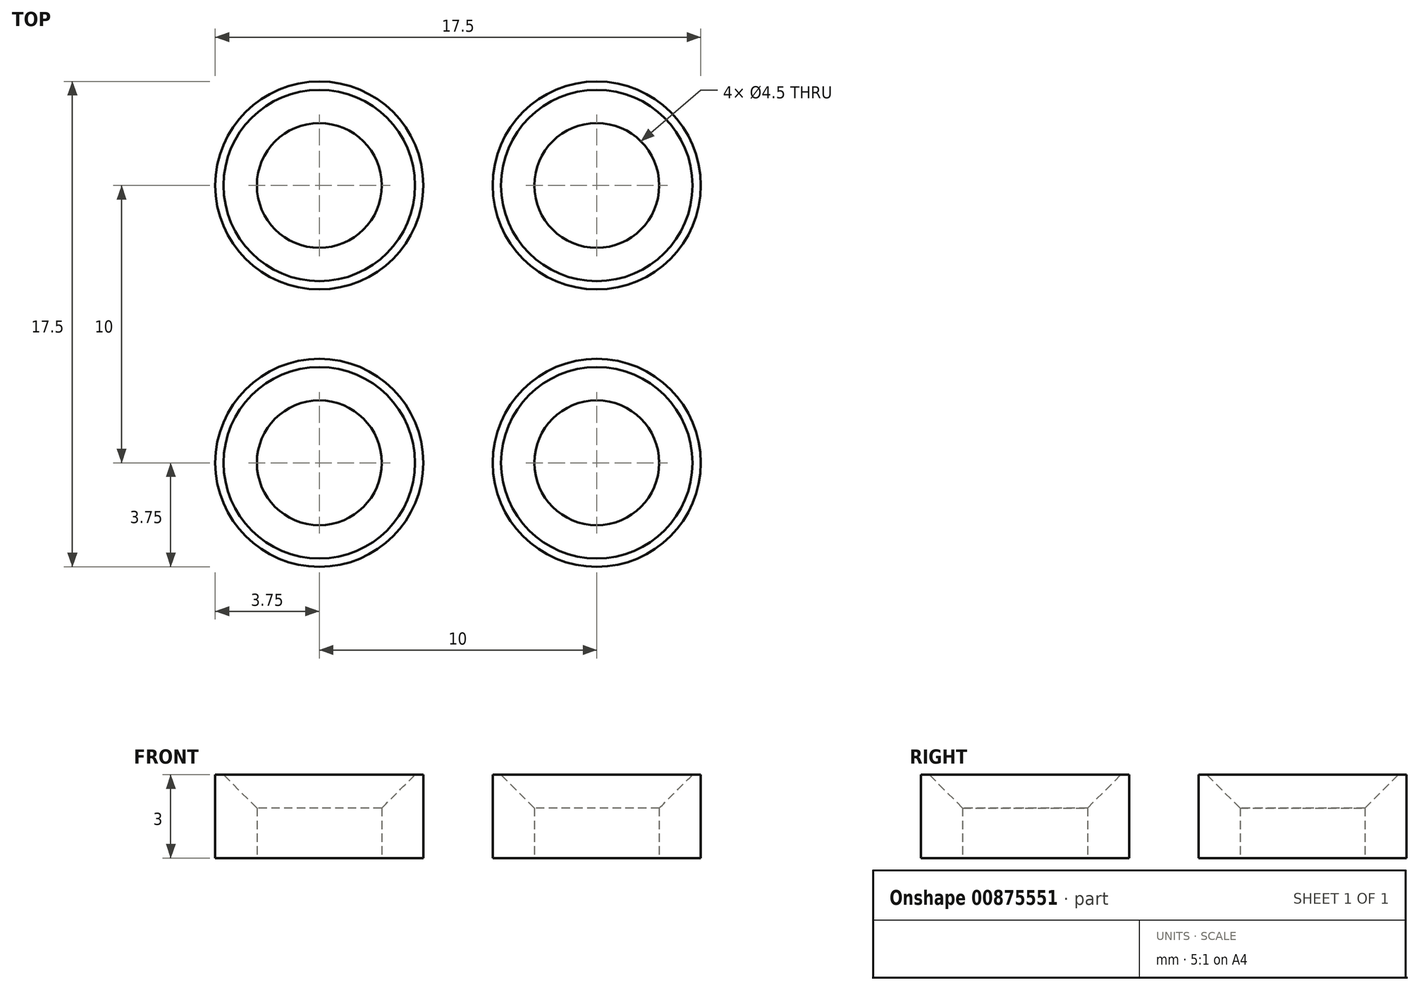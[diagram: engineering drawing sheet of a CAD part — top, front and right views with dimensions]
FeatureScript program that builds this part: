
annotation { "Feature Type Name" : "Feature", "Feature Type Description" : "" }
export const myFeature = defineFeature(function(context is Context, id is Id, definition is map)
    precondition{}
    {
        {
            var Q0;
            Q0=qCreatedBy(makeId("Top.planeOp"),FACE);
            var sketch = newSketch(context, id + "F0", { "sketchPlane" : qUnion([Q0])});
            skCircle(sketch, "E0", {"center": v(0, 0) * mm, "radius": 3.75 * mm});
            skCircle(sketch, "E1", {"center": v(0, 0) * mm, "radius": 2.25 * mm});
            skSolve(sketch);
        }
        {
            var Q0;
            Q0=makeQuery(id+"F0.imprint","IMPRINT",FACE,{"disambiguationData":[TD([[makeQuery(id+"F0.imprint","IMPRINT",EDGE,{"derivedFrom":sQuery(id+"F0.wireOp",EDGE,"E0")}),1.0]])]});
            extrude(context, id + "F1", {"entities" : qUnion([Q0]), "depth" : 3 * mm, "offsetDistance" : 25 * mm});
        }
        {
            var Q0;
            Q0=makeQuery(id+"F1.opExtrude","CAP_EDGE",EDGE,{"disambiguationData":[OSD([sQuery(id+"F0.wireOp",EDGE,"E1")])],"isStart":false});
            chamfer(context, id + "F2", {"entities" : qUnion([Q0]), "width" : 1.2 * mm, "tangentPropagation" : true});
        }
        {
            var Q0;
            Q0=makeQuery(id+"F1.opExtrude","SWEPT_BODY",BODY,{"disambiguationData":[OSD([sQuery(id+"F0.wireOp",EDGE,"E0"),sQuery(id+"F0.wireOp",EDGE,"E1")])]});
            transform(context, id + "F3", {"entities" : qUnion([Q0]), "transformType" : TransformType.TRANSLATION_3D, "dx" : 10 * mm, "dy" : 0 * mm, "dz" : 0 * mm, "makeCopy" : true});
        }
        {
            var Q0;
            Q0=makeQuery(id+"F1.opExtrude","SWEPT_BODY",BODY,{"disambiguationData":[OSD([sQuery(id+"F0.wireOp",EDGE,"E0"),sQuery(id+"F0.wireOp",EDGE,"E1")])]});
            transform(context, id + "F4", {"entities" : qUnion([Q0]), "transformType" : TransformType.TRANSLATION_3D, "dx" : 0 * mm, "dy" : 10 * mm, "dz" : 0 * mm, "makeCopy" : true});
        }
        {
            var Q0;
            Q0=makeQuery(id+"F1.opExtrude","SWEPT_BODY",BODY,{"disambiguationData":[OSD([sQuery(id+"F0.wireOp",EDGE,"E0"),sQuery(id+"F0.wireOp",EDGE,"E1")])]});
            transform(context, id + "F5", {"entities" : qUnion([Q0]), "transformType" : TransformType.TRANSLATION_3D, "dx" : 10 * mm, "dy" : 10 * mm, "dz" : 0 * mm, "makeCopy" : true});
        }
    });
